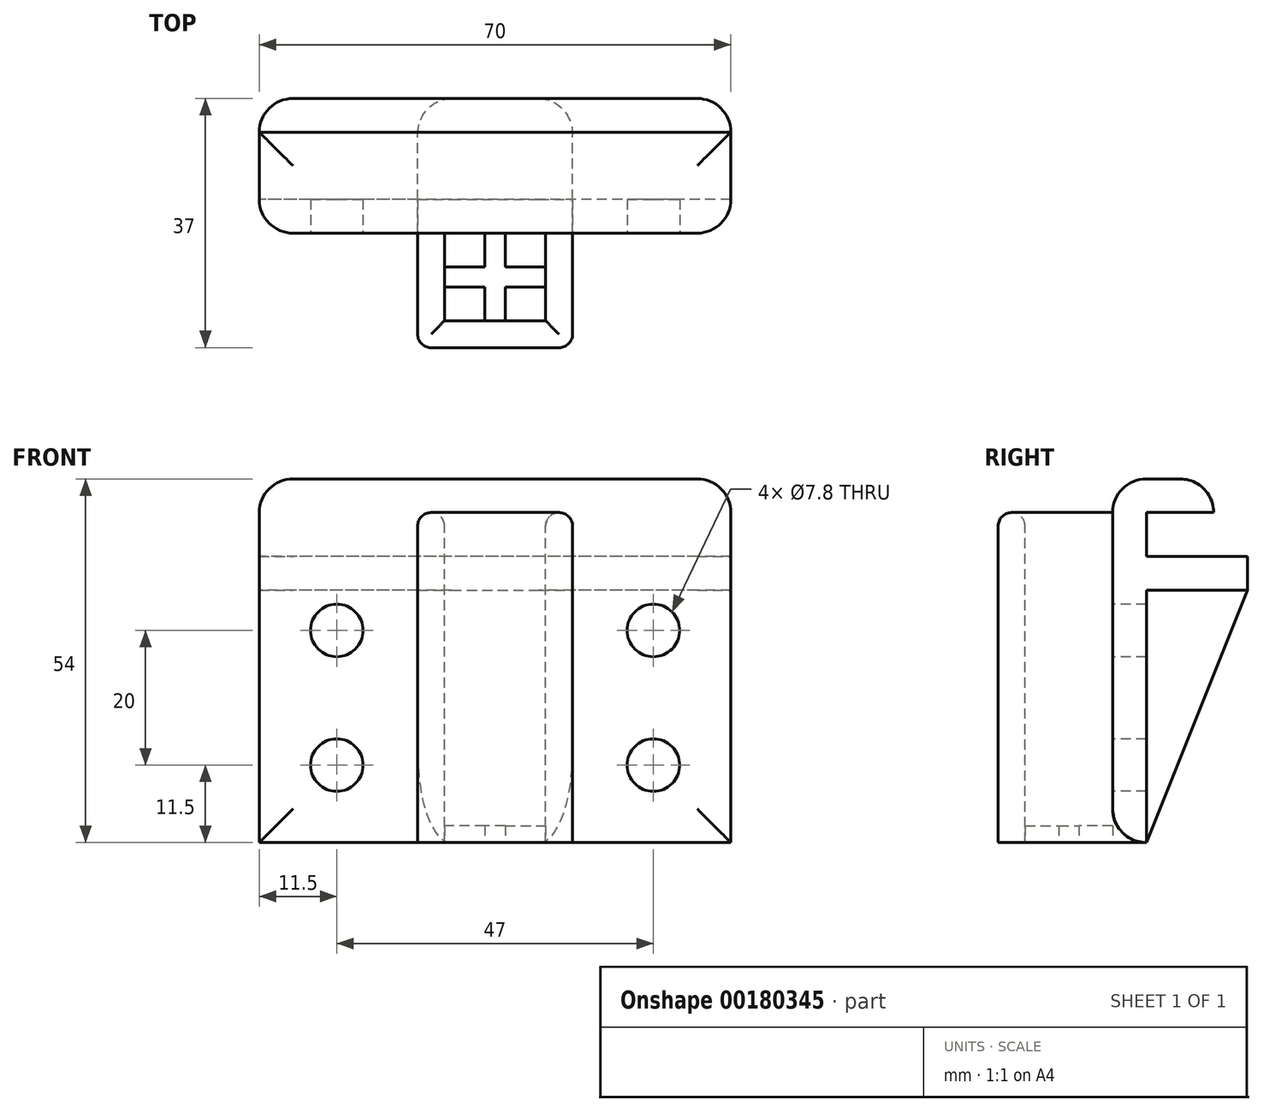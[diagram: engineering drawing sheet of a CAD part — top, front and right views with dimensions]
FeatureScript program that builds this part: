
annotation { "Feature Type Name" : "Feature", "Feature Type Description" : "" }
export const myFeature = defineFeature(function(context is Context, id is Id, definition is map)
    precondition{}
    {
        {
            var Q0;
            Q0=qCreatedBy(makeId("Right.planeOp"),FACE);
            var sketch = newSketch(context, id + "F0", { "sketchPlane" : qUnion([Q0])});
            skLineSegment(sketch, "E0", {"start": v(0, 0) * mm, "end": v(0, 6.5) * mm});
            skLineSegment(sketch, "E1", {"start": v(0, 6.5) * mm, "end": v(10, 6.5) * mm});
            skLineSegment(sketch, "E2", {"start": v(10, 6.5) * mm, "end": v(10, 11.5) * mm});
            skLineSegment(sketch, "E3", {"start": v(10, 11.5) * mm, "end": v(-5, 11.5) * mm});
            skLineSegment(sketch, "E4", {"start": v(-5, 11.5) * mm, "end": v(-5, -5) * mm});
            skLineSegment(sketch, "E5", {"start": v(15, -5) * mm, "end": v(15, 0) * mm});
            skLineSegment(sketch, "E6", {"start": v(15, 0) * mm, "end": v(0, 0) * mm});
            skLineSegment(sketch, "E7", {"start": v(-5, -5) * mm, "end": v(-5, -42.5) * mm});
            skLineSegment(sketch, "E8", {"start": v(-5, -42.5) * mm, "end": v(0, -42.5) * mm});
            skLineSegment(sketch, "E9", {"start": v(0, -42.5) * mm, "end": v(0, -5) * mm});
            skLineSegment(sketch, "E10", {"start": v(15, -5) * mm, "end": v(0, -5) * mm});
            skSolve(sketch);
        }
        {
            var Q0;
            Q0 = qSketchRegion(id + "F0", true);
            extrude(context, id + "F1", {"entities" : qUnion([Q0]), "depth" : 35 * mm, "hasSecondDirection" : true, "secondDirectionOppositeDirection" : true, "secondDirectionDepth" : 35 * mm});
        }
        {
            var Q0;
            Q0=makeQuery(id+"F1.opExtrude","SWEPT_FACE",FACE,{"disambiguationData":[OSD([sQuery(id+"F0.wireOp",EDGE,"E1")])]});
            var sketch = newSketch(context, id + "F2", { "sketchPlane" : qUnion([Q0])});
            skLineSegment(sketch, "E11", {"start": v(7.5, 5) * mm, "end": v(7.5, 18) * mm});
            skLineSegment(sketch, "E12", {"start": v(7.5, 18) * mm, "end": v(0, 18) * mm});
            skLineSegment(sketch, "E13.MirrorCS", {"start": v(-7.5, 5) * mm, "end": v(-7.5, 18) * mm});
            skLineSegment(sketch, "E14.MirrorCS", {"start": v(-7.5, 18) * mm, "end": v(0, 18) * mm});
            skLineSegment(sketch, "E15", {"start": v(0, 22) * mm, "end": v(11.5, 22) * mm});
            skLineSegment(sketch, "E16", {"start": v(11.5, 22) * mm, "end": v(11.5, 5) * mm});
            skLineSegment(sketch, "E17.MirrorCS", {"start": v(0, 22) * mm, "end": v(-11.5, 22) * mm});
            skLineSegment(sketch, "E18.MirrorCS", {"start": v(-11.5, 22) * mm, "end": v(-11.5, 5) * mm});
            skLineSegment(sketch, "E19", {"start": v(7.5, 5) * mm, "end": v(11.5, 5) * mm});
            skLineSegment(sketch, "E20.MirrorCS", {"start": v(-7.5, 5) * mm, "end": v(-11.5, 5) * mm});
            skSolve(sketch);
        }
        {
            var Q0;
            Q0 = qSketchRegion(id + "F2", true);
            var Q1;
            Q1=makeQuery(id+"F1.opExtrude","SWEPT_FACE",FACE,{"disambiguationData":[OSD([sQuery(id+"F0.wireOp",EDGE,"E8")])]});
            extrude(context, id + "F3", {"entities" : qUnion([Q0]), "operationType" : NewBodyOperationType.ADD, "endBound" : BoundingType.UP_TO_SURFACE, "endBoundEntityFace" : qUnion([Q1]), "depth" : 25 * mm});
        }
        {
            var Q0;
            Q0=makeQuery(id+"F3.opExtrude","CAP_EDGE",EDGE,{"disambiguationData":[OSD([sQuery(id+"F2.wireOp",EDGE,"E16")])],"isStart":true});
            var Q1;
            Q1=makeQuery(id+"F3.opExtrude","CAP_EDGE",EDGE,{"disambiguationData":[OSD([sQuery(id+"F2.wireOp",EDGE,"E11")])],"isStart":true});
            var Q2;
            Q2=makeQuery(id+"F3.opExtrude","CAP_EDGE",EDGE,{"disambiguationData":[OSD([sQuery(id+"F2.wireOp",EDGE,"E13.MirrorCS")])],"isStart":true});
            var Q3;
            Q3=makeQuery(id+"F3.opExtrude","CAP_EDGE",EDGE,{"disambiguationData":[OSD([sQuery(id+"F2.wireOp",EDGE,"E12"),sQuery(id+"F2.wireOp",EDGE,"E14.MirrorCS")])],"isStart":true});
            var Q4;
            Q4=makeQuery(id+"F3.opExtrude","CAP_EDGE",EDGE,{"disambiguationData":[OSD([sQuery(id+"F2.wireOp",EDGE,"E15"),sQuery(id+"F2.wireOp",EDGE,"E17.MirrorCS")])],"isStart":true});
            var Q5;
            Q5=makeQuery(id+"F3.opExtrude","CAP_EDGE",EDGE,{"disambiguationData":[OSD([sQuery(id+"F2.wireOp",EDGE,"E18.MirrorCS")])],"isStart":true});
            var Q6;
            Q6=makeQuery(id+"F3.opExtrude","SWEPT_EDGE",EDGE,{"disambiguationData":[OSD([sQuery(id+"F2.wireOp",EDGE,"E17.MirrorCS"),sQuery(id+"F2.wireOp",EDGE,"E18.MirrorCS")])]});
            var Q7;
            Q7=makeQuery(id+"F3.opExtrude","SWEPT_EDGE",EDGE,{"disambiguationData":[OSD([sQuery(id+"F2.wireOp",EDGE,"E15"),sQuery(id+"F2.wireOp",EDGE,"E16")])]});
            fillet(context, id + "F4", {"entities" : qUnion([Q0, Q1, Q2, Q3, Q4, Q5, Q6, Q7]), "radius" : 1.99 * mm, "tangentPropagation" : true, "allowEdgeOverflow" : false});
        }
        {
            var Q0;
            Q0=makeQuery(id+"F1.opExtrude","SWEPT_FACE",FACE,{"disambiguationData":[OSD([sQuery(id+"F0.wireOp",EDGE,"E4"),sQuery(id+"F0.wireOp",EDGE,"E7")])]});
            var sketch = newSketch(context, id + "F5", { "sketchPlane" : qUnion([Q0])});
            skCircle(sketch, "E21", {"center": v(23.5, -11) * mm, "radius": 3.9 * mm});
            skPoint(sketch, "E22", {"position": v(35, -5) * mm});
            skCircle(sketch, "E23", {"center": v(23.5, -31) * mm, "radius": 3.9 * mm});
            skCircle(sketch, "E24.MirrorC", {"center": v(-23.5, -11) * mm, "radius": 3.9 * mm});
            skCircle(sketch, "E25.MirrorC", {"center": v(-23.5, -31) * mm, "radius": 3.9 * mm});
            skSolve(sketch);
        }
        {
            var Q0;
            Q0 = qSketchRegion(id + "F5", true);
            extrude(context, id + "F6", {"entities" : qUnion([Q0]), "operationType" : NewBodyOperationType.REMOVE, "oppositeDirection" : true, "depth" : 25 * mm});
        }
        {
            var Q0;
            Q0=makeQuery(id+"F3.boolean.opBoolean","MERGE",FACE,{"derivedFrom":[makeQuery(id+"F1.opExtrude","SWEPT_FACE",FACE,{"disambiguationData":[OSD([sQuery(id+"F0.wireOp",EDGE,"E8")])]}),makeQuery(id+"F3.opExtrude","CAP_FACE",FACE,{"disambiguationData":[OSD([sQuery(id+"F2.wireOp",EDGE,"E11"),sQuery(id+"F2.wireOp",EDGE,"E12"),sQuery(id+"F2.wireOp",EDGE,"E13.MirrorCS"),sQuery(id+"F2.wireOp",EDGE,"E14.MirrorCS"),sQuery(id+"F2.wireOp",EDGE,"E15"),sQuery(id+"F2.wireOp",EDGE,"E16"),sQuery(id+"F2.wireOp",EDGE,"E17.MirrorCS"),sQuery(id+"F2.wireOp",EDGE,"E18.MirrorCS"),sQuery(id+"F2.wireOp",EDGE,"E19"),sQuery(id+"F2.wireOp",EDGE,"E20.MirrorCS")])],"isStart":false})]});
            var sketch = newSketch(context, id + "F7", { "sketchPlane" : qUnion([Q0])});
            skPoint(sketch, "E26", {"position": v(-7.5, 11.5) * mm});
            skLineSegment(sketch, "E27", {"start": v(-7.5, 11.5) * mm, "end": v(0, 11.5) * mm, "construction": true});
            skLineSegment(sketch, "E28", {"start": v(0, 18) * mm, "end": v(1.5, 18) * mm});
            skLineSegment(sketch, "E29", {"start": v(1.5, 18) * mm, "end": v(1.5, 13) * mm});
            skLineSegment(sketch, "E30", {"start": v(1.5, 13) * mm, "end": v(7.5, 13) * mm});
            skLineSegment(sketch, "E31", {"start": v(7.5, 13) * mm, "end": v(7.5, 11.5) * mm});
            skLineSegment(sketch, "E32.MirrorCS", {"start": v(0, 18) * mm, "end": v(-1.5, 18) * mm});
            skLineSegment(sketch, "E33.MirrorCS", {"start": v(-1.5, 18) * mm, "end": v(-1.5, 13) * mm});
            skLineSegment(sketch, "E34.MirrorCS", {"start": v(-1.5, 13) * mm, "end": v(-7.5, 13) * mm});
            skLineSegment(sketch, "E35.MirrorCS", {"start": v(-7.5, 13) * mm, "end": v(-7.5, 11.5) * mm});
            skLineSegment(sketch, "E36.MirrorCS", {"start": v(-7.5, 10) * mm, "end": v(-7.5, 11.5) * mm});
            skLineSegment(sketch, "E37.MirrorCS", {"start": v(-1.5, 10) * mm, "end": v(-7.5, 10) * mm});
            skLineSegment(sketch, "E38.MirrorCS", {"start": v(-1.5, 5) * mm, "end": v(-1.5, 10) * mm});
            skLineSegment(sketch, "E39.MirrorCS", {"start": v(0, 5) * mm, "end": v(-1.5, 5) * mm});
            skLineSegment(sketch, "E40.MirrorCS", {"start": v(0, 5) * mm, "end": v(1.5, 5) * mm});
            skLineSegment(sketch, "E41.MirrorCS", {"start": v(1.5, 5) * mm, "end": v(1.5, 10) * mm});
            skLineSegment(sketch, "E42.MirrorCS", {"start": v(1.5, 10) * mm, "end": v(7.5, 10) * mm});
            skLineSegment(sketch, "E43.MirrorCS", {"start": v(7.5, 10) * mm, "end": v(7.5, 11.5) * mm});
            skSolve(sketch);
        }
        {
            var Q0;
            Q0 = qSketchRegion(id + "F7", true);
            extrude(context, id + "F8", {"entities" : qUnion([Q0]), "operationType" : NewBodyOperationType.ADD, "oppositeDirection" : true, "depth" : 2.5 * mm});
        }
        {
            var Q0;
            Q0=qCreatedBy(makeId("Right.planeOp"),FACE);
            var sketch = newSketch(context, id + "F9", { "sketchPlane" : qUnion([Q0])});
            skLineSegment(sketch, "E44", {"start": v(0, -42.5) * mm, "end": v(15, -5) * mm});
            skLineSegment(sketch, "E45", {"start": v(15, -5) * mm, "end": v(0, -5) * mm});
            skLineSegment(sketch, "E46", {"start": v(0, -5) * mm, "end": v(0, -42.5) * mm});
            skSolve(sketch);
        }
        {
            var Q0;
            Q0 = qSketchRegion(id + "F9", true);
            var Q1;
            Q1=makeQuery(id+"F3.opExtrude","SWEPT_FACE",FACE,{"disambiguationData":[OSD([sQuery(id+"F2.wireOp",EDGE,"E18.MirrorCS")])]});
            var Q2;
            Q2=makeQuery(id+"F3.opExtrude","SWEPT_FACE",FACE,{"disambiguationData":[OSD([sQuery(id+"F2.wireOp",EDGE,"E16")])]});
            extrude(context, id + "F10", {"entities" : qUnion([Q0]), "operationType" : NewBodyOperationType.ADD, "endBound" : BoundingType.UP_TO_SURFACE, "oppositeDirection" : true, "endBoundEntityFace" : qUnion([Q1]), "depth" : 25 * mm, "hasSecondDirection" : true, "secondDirectionBound" : BoundingType.UP_TO_SURFACE, "secondDirectionOppositeDirection" : false, "secondDirectionBoundEntityFace" : qUnion([Q2]), "secondDirectionDepth" : 25 * mm});
        }
        {
            var Q0;
            {var subQ0=sQuery(id+"F2.wireOp",EDGE,"E18.MirrorCS");var subQ1=sQuery(id+"F0.wireOp",EDGE,"E8");var subQ2=sQuery(id+"F0.wireOp",EDGE,"E7");Q0=makeQuery(id+"F3.boolean.opBoolean","SPLIT",EDGE,{"disambiguationData":[TD([makeQuery(id+"F3.opExtrude","SWEPT_FACE",FACE,{"disambiguationData":[OSD([subQ0])]})])],"derivedFrom":makeQuery(id+"F1.opExtrude","SWEPT_EDGE",EDGE,{"disambiguationData":[OSD([subQ2,subQ1])]})});}
            var Q1;
            {var subQ0=sQuery(id+"F2.wireOp",EDGE,"E16");var subQ1=sQuery(id+"F0.wireOp",EDGE,"E8");var subQ2=sQuery(id+"F0.wireOp",EDGE,"E7");Q1=makeQuery(id+"F3.boolean.opBoolean","SPLIT",EDGE,{"disambiguationData":[TD([makeQuery(id+"F3.opExtrude","SWEPT_FACE",FACE,{"disambiguationData":[OSD([subQ0])]})])],"derivedFrom":makeQuery(id+"F1.opExtrude","SWEPT_EDGE",EDGE,{"disambiguationData":[OSD([subQ2,subQ1])]})});}
            var Q2;
            Q2=makeQuery(id+"F1.opExtrude","SWEPT_EDGE",EDGE,{"disambiguationData":[OSD([sQuery(id+"F0.wireOp",EDGE,"E2"),sQuery(id+"F0.wireOp",EDGE,"E3")])]});
            var Q3;
            Q3=makeQuery(id+"F1.opExtrude","CAP_EDGE",EDGE,{"disambiguationData":[OSD([sQuery(id+"F0.wireOp",EDGE,"E3")])],"isStart":false});
            var Q4;
            Q4=makeQuery(id+"F1.opExtrude","CAP_EDGE",EDGE,{"disambiguationData":[OSD([sQuery(id+"F0.wireOp",EDGE,"E3")])],"isStart":true});
            var Q5;
            Q5=makeQuery(id+"F1.opExtrude","SWEPT_EDGE",EDGE,{"disambiguationData":[OSD([sQuery(id+"F0.wireOp",EDGE,"E3"),sQuery(id+"F0.wireOp",EDGE,"E4")])]});
            var Q6;
            Q6=makeQuery(id+"F1.opExtrude","CAP_EDGE",EDGE,{"disambiguationData":[OSD([sQuery(id+"F0.wireOp",EDGE,"E4"),sQuery(id+"F0.wireOp",EDGE,"E7")])],"isStart":true});
            var Q7;
            Q7=makeQuery(id+"F1.opExtrude","CAP_EDGE",EDGE,{"disambiguationData":[OSD([sQuery(id+"F0.wireOp",EDGE,"E4"),sQuery(id+"F0.wireOp",EDGE,"E7")])],"isStart":false});
            var Q8;
            Q8=makeQuery(id+"F10.opExtrude","CAP_EDGE",EDGE,{"disambiguationData":[OSD([sQuery(id+"F9.wireOp",EDGE,"E44")])],"isStart":true});
            var Q9;
            Q9=makeQuery(id+"F10.opExtrude","CAP_EDGE",EDGE,{"disambiguationData":[OSD([sQuery(id+"F9.wireOp",EDGE,"E44")])],"isStart":false});
            var Q10;
            Q10=makeQuery(id+"F1.opExtrude","CAP_EDGE",EDGE,{"disambiguationData":[OSD([sQuery(id+"F0.wireOp",EDGE,"E5")])],"isStart":false});
            var Q11;
            Q11=makeQuery(id+"F1.opExtrude","CAP_EDGE",EDGE,{"disambiguationData":[OSD([sQuery(id+"F0.wireOp",EDGE,"E5")])],"isStart":true});
            fillet(context, id + "F11", {"entities" : qUnion([Q0, Q1, Q2, Q3, Q4, Q5, Q6, Q7, Q8, Q9, Q10, Q11]), "radius" : 5 * mm, "tangentPropagation" : true, "allowEdgeOverflow" : false});
        }
    });
